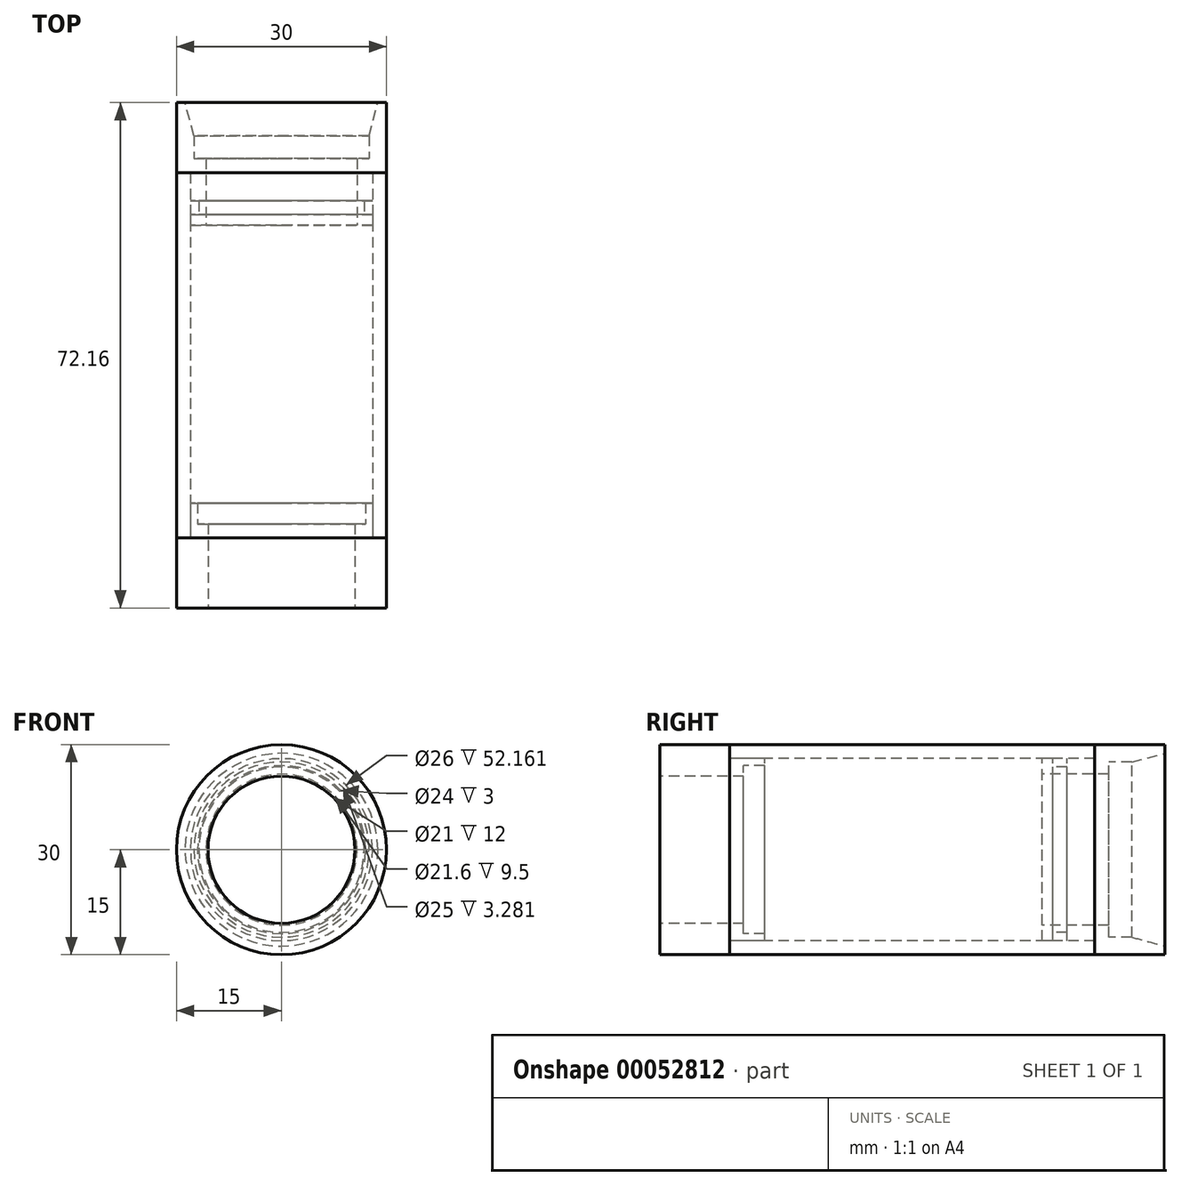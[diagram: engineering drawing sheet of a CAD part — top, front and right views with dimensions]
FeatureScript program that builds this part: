
annotation { "Feature Type Name" : "Feature", "Feature Type Description" : "" }
export const myFeature = defineFeature(function(context is Context, id is Id, definition is map)
    precondition{}
    {
        {
            var Q0;
            Q0=qCreatedBy(makeId("Right.planeOp"),FACE);
            var sketch = newSketch(context, id + "F0", { "sketchPlane" : qUnion([Q0])});
            skLineSegment(sketch, "E0", {"start": v(0, 0) * mm, "end": v(0, 12) * mm});
            skLineSegment(sketch, "E1", {"start": v(0, 12) * mm, "end": v(-3, 12) * mm});
            skLineSegment(sketch, "E2", {"start": v(0, 0) * mm, "end": v(-3, 0) * mm});
            skPoint(sketch, "E3.orphan", {"position": v(-3, -12) * mm});
            skLineSegment(sketch, "E4", {"start": v(-3, 12) * mm, "end": v(-3, 0) * mm});
            skLineSegment(sketch, "E5", {"start": v(0, 0) * mm, "end": v(29.49, 0) * mm, "construction": true});
            skLineSegment(sketch, "E6.top", {"start": v(-5, 13) * mm, "end": v(47.16, 13) * mm});
            skLineSegment(sketch, "E6.right", {"start": v(47.16, 15) * mm, "end": v(47.16, 13) * mm});
            skLineSegment(sketch, "E7", {"start": v(-15, 15) * mm, "end": v(-15, 10.5) * mm});
            skLineSegment(sketch, "E8", {"start": v(-15, 10.5) * mm, "end": v(-3, 10.5) * mm});
            skLineSegment(sketch, "E9", {"start": v(0, 12) * mm, "end": v(0, 13) * mm});
            skLineSegment(sketch, "E10", {"start": v(0, 12) * mm, "end": v(0, 12) * mm});
            skLineSegment(sketch, "E11", {"start": v(-5, 13) * mm, "end": v(-5, 15) * mm});
            skLineSegment(sketch, "E12", {"start": v(-5, 15) * mm, "end": v(47.16, 15) * mm});
            skLineSegment(sketch, "E13", {"start": v(49.16, 10.8) * mm, "end": v(39.66, 10.8) * mm});
            skLineSegment(sketch, "E14", {"start": v(39.66, 10.8) * mm, "end": v(39.66, 13) * mm});
            skLineSegment(sketch, "E15", {"start": v(41.16, 13) * mm, "end": v(41.16, 11.8) * mm});
            skLineSegment(sketch, "E16", {"start": v(41.16, 11.8) * mm, "end": v(43.16, 11.8) * mm});
            skLineSegment(sketch, "E17", {"start": v(43.16, 11.8) * mm, "end": v(43.16, 13) * mm});
            skArc(sketch, "E18", {"start": v(49.56, 12.5) * mm, "mid": v(48.4, 6.3) * mm, "end": v(48, 0) * mm});
            skPoint(sketch, "E19", {"position": v(14.74, 0) * mm});
            skArc(sketch, "E20", {"start": v(53, 0) * mm, "mid": v(52.61, 6.3) * mm, "end": v(51.44, 12.5) * mm});
            skLineSegment(sketch, "E21", {"start": v(49.16, 10.8) * mm, "end": v(49.16, 12.5) * mm});
            skLineSegment(sketch, "E22", {"start": v(49.16, 12.5) * mm, "end": v(49.56, 12.5) * mm});
            skLineSegment(sketch, "E23", {"start": v(48, 0) * mm, "end": v(53, 0) * mm});
            skLineSegment(sketch, "E24", {"start": v(51.44, 12.5) * mm, "end": v(52.44, 12.5) * mm});
            skLineSegment(sketch, "E25", {"start": v(52.44, 12.5) * mm, "end": v(57.16, 13.76) * mm});
            skLineSegment(sketch, "E26", {"start": v(-15, 15) * mm, "end": v(-5, 15) * mm});
            skLineSegment(sketch, "E27", {"start": v(47.16, 15) * mm, "end": v(57.16, 15) * mm});
            skLineSegment(sketch, "E28", {"start": v(57.16, 15) * mm, "end": v(57.16, 13.76) * mm});
            skLineSegment(sketch, "E29", {"start": v(49.56, 12.5) * mm, "end": v(51.44, 12.5) * mm});
            skSolve(sketch);
        }
        {
            var Q0;
            {var subQ5=sQuery(id+"F0.wireOp",EDGE,"E1");Q0=makeQuery(id+"F0.imprint","IMPRINT",FACE,{"disambiguationData":[TD([[makeQuery(id+"F0.imprint","IMPRINT",EDGE,{"derivedFrom":subQ5}),-1.0]])]});}
            var Q1;
            {var subQ2=sQuery(id+"F0.wireOp",EDGE,"E6.right");Q1=makeQuery(id+"F0.imprint","IMPRINT",FACE,{"disambiguationData":[TD([[makeQuery(id+"F0.imprint","IMPRINT",EDGE,{"derivedFrom":subQ2}),1.0]])]});}
            var Q2;
            Q2=sQuery(id+"F0.wireOp",EDGE,"E5");
            revolve(context, id + "F1", {"entities" : qUnion([Q0, Q1]), "axis" : qUnion([Q2]), "revolveType" : RevolveType.FULL});
        }
        {
            var Q0;
            {var subQ6=sQuery(id+"F0.wireOp",EDGE,"E6.right");Q0=makeQuery(id+"F0.imprint","IMPRINT",FACE,{"disambiguationData":[TD([[makeQuery(id+"F0.imprint","IMPRINT",EDGE,{"derivedFrom":subQ6}),-1.0]])]});}
            var Q1;
            Q1=sQuery(id+"F0.wireOp",EDGE,"E5");
            revolve(context, id + "F2", {"entities" : qUnion([Q0]), "axis" : qUnion([Q1]), "revolveType" : RevolveType.FULL});
        }
    });
